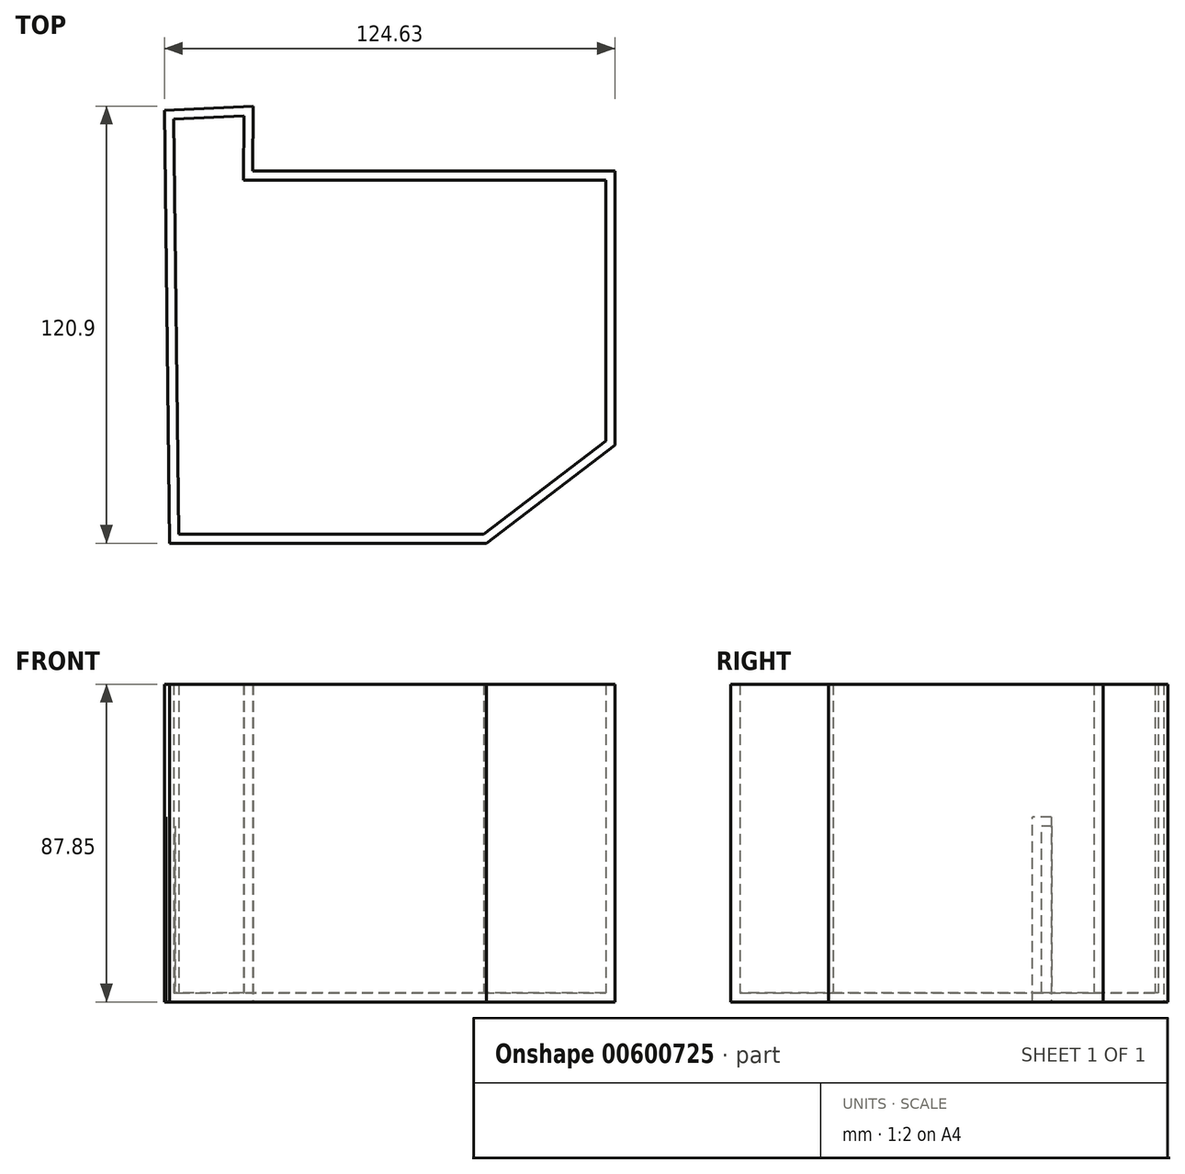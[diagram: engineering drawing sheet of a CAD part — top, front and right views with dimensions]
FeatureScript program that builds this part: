
annotation { "Feature Type Name" : "Feature", "Feature Type Description" : "" }
export const myFeature = defineFeature(function(context is Context, id is Id, definition is map)
    precondition{}
    {
        {
            var Q0;
            Q0=qCreatedBy(makeId("Top.planeOp"),FACE);
            var sketch = newSketch(context, id + "F0", { "sketchPlane" : qUnion([Q0])});
            skLineSegment(sketch, "E0", {"start": v(-64.04, 65.4) * mm, "end": v(-62.55, -54.4) * mm});
            skLineSegment(sketch, "E1", {"start": v(-62.55, -54.4) * mm, "end": v(25.07, -54.4) * mm});
            skLineSegment(sketch, "E2", {"start": v(25.07, -54.4) * mm, "end": v(60.6, -27.3) * mm});
            skLineSegment(sketch, "E3", {"start": v(60.6, -27.3) * mm, "end": v(60.6, 48.6) * mm});
            skLineSegment(sketch, "E4", {"start": v(60.6, 48.6) * mm, "end": v(-39.6, 48.6) * mm});
            skLineSegment(sketch, "E5", {"start": v(-39.6, 48.6) * mm, "end": v(-39.52, 66.5) * mm});
            skLineSegment(sketch, "E6", {"start": v(-39.52, 66.5) * mm, "end": v(-64.04, 65.4) * mm});
            skSolve(sketch);
        }
        {
            var Q0;
            Q0 = qSketchRegion(id + "F0", true);
            extrude(context, id + "F1", {"entities" : qUnion([Q0]), "depth" : 62.45 * mm, "offsetDistance" : 25.4 * mm});
        }
        {
            var Q0;
            Q0=qCreatedBy(makeId("Top.planeOp"),FACE);
            var sketch = newSketch(context, id + "F2", { "sketchPlane" : qUnion([Q0])});
            skLineSegment(sketch, "E7.bottom", {"start": v(-63.66, 48.4) * mm, "end": v(-3.32, 48.4) * mm});
            skLineSegment(sketch, "E7.top", {"start": v(-63.66, 29.1) * mm, "end": v(-3.32, 29.1) * mm});
            skLineSegment(sketch, "E7.left", {"start": v(-63.66, 48.4) * mm, "end": v(-63.66, 29.1) * mm});
            skLineSegment(sketch, "E7.right", {"start": v(-3.32, 48.4) * mm, "end": v(-3.32, 29.1) * mm});
            skSolve(sketch);
        }
        {
            var Q0;
            Q0=qCreatedBy(makeId("Top.planeOp"),FACE);
            var sketch = newSketch(context, id + "F3", { "sketchPlane" : qUnion([Q0])});
            skLineSegment(sketch, "E8.bottom", {"start": v(-62.4, -54.52) * mm, "end": v(-53.36, -54.52) * mm});
            skLineSegment(sketch, "E8.top", {"start": v(-62.4, 29.7) * mm, "end": v(-53.36, 29.7) * mm});
            skLineSegment(sketch, "E8.left", {"start": v(-62.4, -54.52) * mm, "end": v(-62.4, 29.7) * mm});
            skLineSegment(sketch, "E8.right", {"start": v(-53.36, -54.52) * mm, "end": v(-53.36, 29.7) * mm});
            skLineSegment(sketch, "E9.bottom", {"start": v(24.96, -54.42) * mm, "end": v(-53.36, -54.42) * mm});
            skLineSegment(sketch, "E9.top", {"start": v(24.96, -40.8) * mm, "end": v(-53.36, -40.8) * mm});
            skLineSegment(sketch, "E9.left", {"start": v(24.96, -54.42) * mm, "end": v(24.96, -40.8) * mm});
            skLineSegment(sketch, "E9.right", {"start": v(-53.36, -54.42) * mm, "end": v(-53.36, -40.8) * mm});
            skSolve(sketch);
        }
        {
            var Q0;
            Q0=makeQuery(id+"F2.imprint","IMPRINT",FACE,{"disambiguationData":[TD([[makeQuery(id+"F2.imprint","IMPRINT",EDGE,{"derivedFrom":sQuery(id+"F2.wireOp",EDGE,"E7.bottom")}),-1.0]])]});
            var Q1;
            Q1=sQuery(id+"F3.wireOp",EDGE,"E8.right");
            var Q2;
            Q2=sQuery(id+"F2.wireOp",EDGE,"E7.top");
            var Q3;
            Q3=sQuery(id+"F2.wireOp",EDGE,"E7.right");
            var Q4;
            Q4=sQuery(id+"F3.wireOp",EDGE,"E9.top");
            var Q5;
            Q5=sQuery(id+"F3.wireOp",EDGE,"E9.left");
            var Q6;
            Q6=sQuery(id+"F3.wireOp",EDGE,"E9.bottom");
            var Q7;
            Q7=sQuery(id+"F3.wireOp",EDGE,"E8.left");
            var Q8;
            Q8=sQuery(id+"F3.wireOp",EDGE,"E8.bottom");
            var Q9;
            Q9=sQuery(id+"F2.wireOp",EDGE,"E7.bottom");
            var Q10;
            Q10=sQuery(id+"F2.wireOp",EDGE,"E7.left");
            extrude(context, id + "F4", {"entities" : qUnion([Q0]), "operationType" : NewBodyOperationType.ADD, "surfaceEntities" : qUnion([Q1, Q2, Q3, Q4, Q5, Q6, Q7, Q8, Q9, Q10]), "depth" : 51.16 * mm, "offsetDistance" : 25.4 * mm});
        }
        {
            var Q0;
            Q0=makeQuery(id+"F1.opExtrude","CAP_FACE",FACE,{"disambiguationData":[OSD([sQuery(id+"F0.wireOp",EDGE,"E0"),sQuery(id+"F0.wireOp",EDGE,"E1"),sQuery(id+"F0.wireOp",EDGE,"E2"),sQuery(id+"F0.wireOp",EDGE,"E3"),sQuery(id+"F0.wireOp",EDGE,"E4"),sQuery(id+"F0.wireOp",EDGE,"E5"),sQuery(id+"F0.wireOp",EDGE,"E6")])],"isStart":false});
            extrude(context, id + "F5", {"entities" : qUnion([Q0]), "operationType" : NewBodyOperationType.ADD, "depth" : 25.4 * mm, "offsetDistance" : 25.4 * mm});
        }
        {
            var Q0;
            Q0=makeQuery(id+"F5.opExtrude","CAP_FACE",FACE,{"disambiguationData":[OSD([sQuery(id+"F0.wireOp",EDGE,"E0"),sQuery(id+"F0.wireOp",EDGE,"E1"),sQuery(id+"F0.wireOp",EDGE,"E2"),sQuery(id+"F0.wireOp",EDGE,"E3"),sQuery(id+"F0.wireOp",EDGE,"E4"),sQuery(id+"F0.wireOp",EDGE,"E5"),sQuery(id+"F0.wireOp",EDGE,"E6")])],"isStart":false});
            shell(context, id + "F6", {"entities" : qUnion([Q0]), "thickness" : 2.54 * mm});
        }
    });
